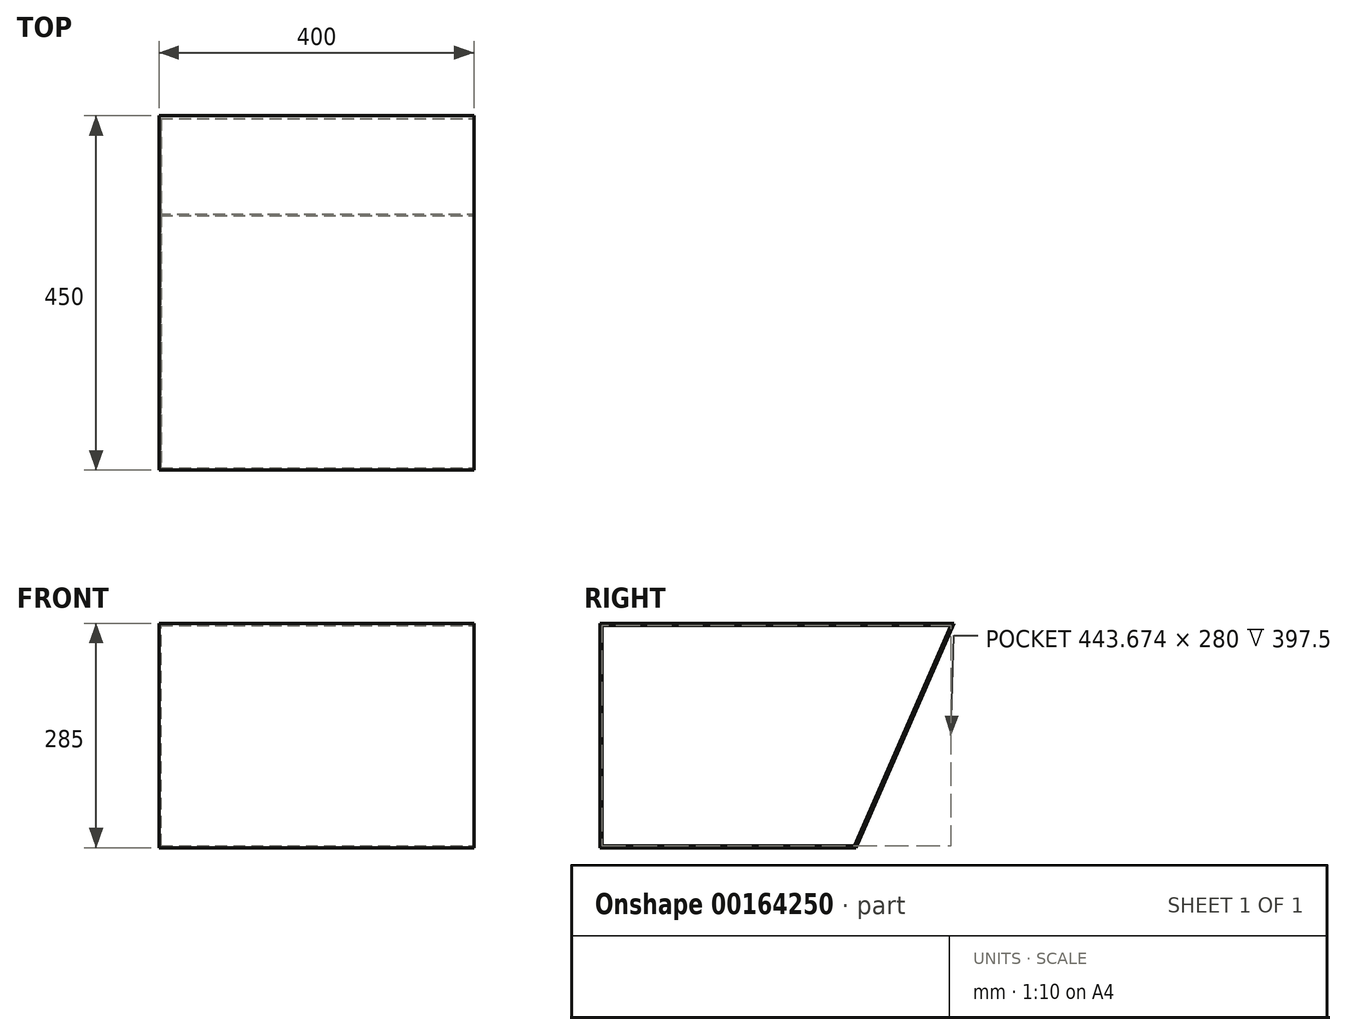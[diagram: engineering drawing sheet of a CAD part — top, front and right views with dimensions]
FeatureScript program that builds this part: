
annotation { "Feature Type Name" : "Feature", "Feature Type Description" : "" }
export const myFeature = defineFeature(function(context is Context, id is Id, definition is map)
    precondition{}
    {
        {
            var Q0;
            Q0=qCreatedBy(makeId("Right.planeOp"),FACE);
            var sketch = newSketch(context, id + "F0", { "sketchPlane" : qUnion([Q0])});
            skLineSegment(sketch, "E0", {"start": v(-163.31, 183.3) * mm, "end": v(286.69, 183.3) * mm});
            skLineSegment(sketch, "E1", {"start": v(286.69, 183.3) * mm, "end": v(161.69, -101.7) * mm});
            skLineSegment(sketch, "E2", {"start": v(161.69, -101.7) * mm, "end": v(-163.31, -101.7) * mm});
            skLineSegment(sketch, "E3", {"start": v(-163.31, -101.7) * mm, "end": v(-163.31, 183.3) * mm});
            skSolve(sketch);
        }
        {
            var Q0;
            Q0 = qSketchRegion(id + "F0", true);
            extrude(context, id + "F1", {"entities" : qUnion([Q0]), "oppositeDirection" : true, "depth" : 400 * mm});
        }
        {
            var Q0;
            Q0=makeQuery(id+"F1.opExtrude","CAP_FACE",FACE,{"disambiguationData":[OSD([sQuery(id+"F0.wireOp",EDGE,"E0"),sQuery(id+"F0.wireOp",EDGE,"E1"),sQuery(id+"F0.wireOp",EDGE,"E2"),sQuery(id+"F0.wireOp",EDGE,"E3")])],"isStart":true});
            shell(context, id + "F2", {"entities" : qUnion([Q0]), "thickness" : 2.5 * mm});
        }
    });
